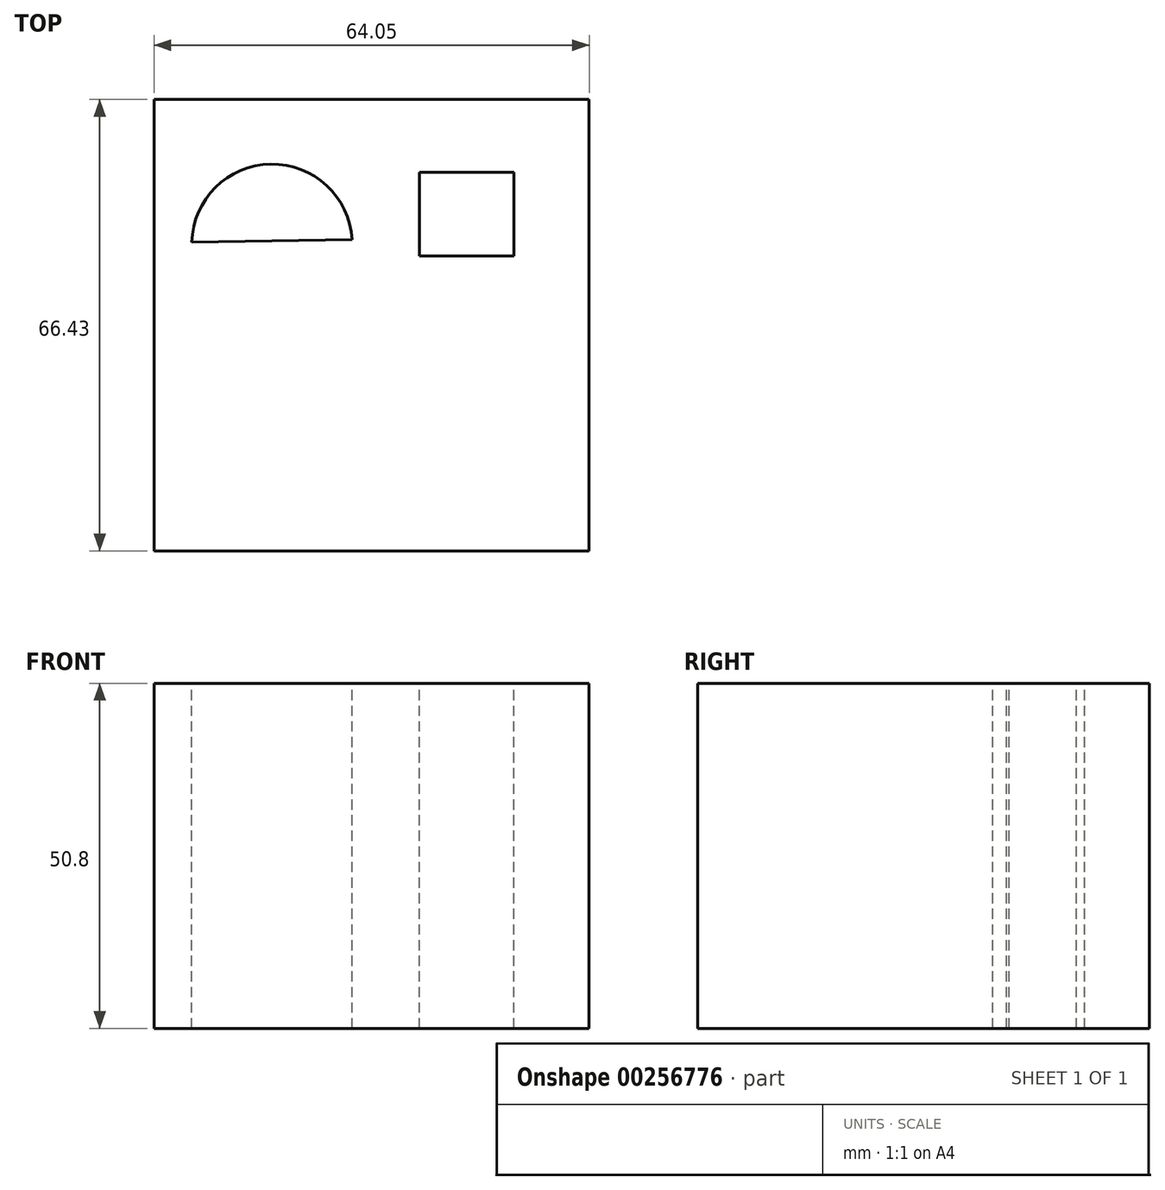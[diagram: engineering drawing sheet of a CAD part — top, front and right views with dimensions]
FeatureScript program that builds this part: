
annotation { "Feature Type Name" : "Feature", "Feature Type Description" : "" }
export const myFeature = defineFeature(function(context is Context, id is Id, definition is map)
    precondition{}
    {
        {
            var Q0;
            Q0=qCreatedBy(makeId("Top.planeOp"),FACE);
            var sketch = newSketch(context, id + "F0", { "sketchPlane" : qUnion([Q0])});
            skLineSegment(sketch, "E0.bottom", {"start": v(-33.51, 36.39) * mm, "end": v(30.54, 36.39) * mm});
            skLineSegment(sketch, "E0.top", {"start": v(-33.51, -30.04) * mm, "end": v(30.54, -30.04) * mm});
            skLineSegment(sketch, "E0.left", {"start": v(-33.51, 36.39) * mm, "end": v(-33.51, -30.04) * mm});
            skLineSegment(sketch, "E0.right", {"start": v(30.54, 36.39) * mm, "end": v(30.54, -30.04) * mm});
            skSolve(sketch);
        }
        {
            var Q0;
            Q0=makeQuery(id+"F0.imprint","IMPRINT",FACE,{"disambiguationData":[TD([[makeQuery(id+"F0.imprint","IMPRINT",EDGE,{"derivedFrom":sQuery(id+"F0.wireOp",EDGE,"E0.bottom")}),-1.0]])]});
            extrude(context, id + "F1", {"entities" : qUnion([Q0]), "depth" : 50.8 * mm});
        }
        {
            var Q0;
            Q0=makeQuery(id+"F1.opExtrude","CAP_FACE",FACE,{"disambiguationData":[OSD([sQuery(id+"F0.wireOp",EDGE,"E0.bottom"),sQuery(id+"F0.wireOp",EDGE,"E0.top"),sQuery(id+"F0.wireOp",EDGE,"E0.left"),sQuery(id+"F0.wireOp",EDGE,"E0.right")])],"isStart":false});
            var sketch = newSketch(context, id + "F2", { "sketchPlane" : qUnion([Q0])});
            skLineSegment(sketch, "E1.bottom", {"start": v(5.55, 25.68) * mm, "end": v(19.43, 25.68) * mm});
            skLineSegment(sketch, "E1.top", {"start": v(5.55, 13.38) * mm, "end": v(19.43, 13.38) * mm});
            skLineSegment(sketch, "E1.left", {"start": v(5.55, 25.68) * mm, "end": v(5.55, 13.38) * mm});
            skLineSegment(sketch, "E1.right", {"start": v(19.43, 25.68) * mm, "end": v(19.43, 13.38) * mm});
            skSolve(sketch);
        }
        {
            var Q0;
            Q0 = qSketchRegion(id + "F2", true);
            extrude(context, id + "F3", {"entities" : qUnion([Q0]), "operationType" : NewBodyOperationType.REMOVE, "oppositeDirection" : true, "depth" : 50.8 * mm});
        }
        {
            var Q0;
            Q0=makeQuery(id+"F1.opExtrude","CAP_FACE",FACE,{"disambiguationData":[OSD([sQuery(id+"F0.wireOp",EDGE,"E0.bottom"),sQuery(id+"F0.wireOp",EDGE,"E0.top"),sQuery(id+"F0.wireOp",EDGE,"E0.left"),sQuery(id+"F0.wireOp",EDGE,"E0.right")])],"isStart":false});
            var sketch = newSketch(context, id + "F4", { "sketchPlane" : qUnion([Q0])});
            skArc(sketch, "E2", {"start": v(-4.36, 15.76) * mm, "mid": v(-16.35, 26.89) * mm, "end": v(-27.96, 15.37) * mm});
            skLineSegment(sketch, "E3", {"start": v(-27.96, 15.37) * mm, "end": v(-4.36, 15.76) * mm});
            skSolve(sketch);
        }
        {
            var Q0;
            Q0=makeQuery(id+"F4.imprint","IMPRINT",FACE,{"disambiguationData":[TD([[makeQuery(id+"F4.imprint","IMPRINT",EDGE,{"derivedFrom":sQuery(id+"F4.wireOp",EDGE,"E2")}),1.0]])]});
            extrude(context, id + "F5", {"entities" : qUnion([Q0]), "operationType" : NewBodyOperationType.REMOVE, "oppositeDirection" : true, "depth" : 50.8 * mm});
        }
    });
